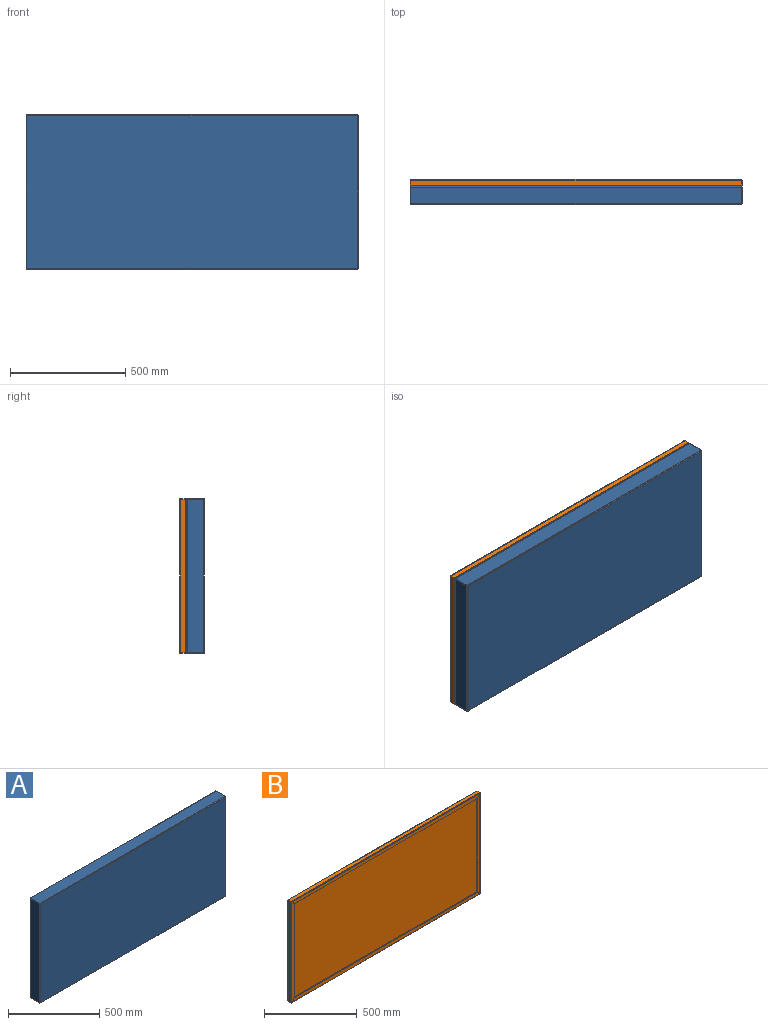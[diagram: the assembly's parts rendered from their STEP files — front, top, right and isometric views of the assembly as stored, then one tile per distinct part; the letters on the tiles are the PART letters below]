
ASSEMBLY  parts=2 mates=1
PART A: 78 faces, bbox 1439x79x669 mm
  f0: plane 2.28x2mm, normal (0,-1,0), area 4.6mm2, adj f3,f4,f5,f7
  f1: plane 2.28x2mm, normal (0,-1,0), area 4.6mm2, adj f2,f4,f5,f6
  f2: plane 70.4x2mm, normal (-1,0,0), area 140.8mm2, adj f1,f4,f5,f36
  f3: plane 70.4x2mm, normal (1,0,0), area 140.8mm2, adj f0,f4,f5,f37
  f4: plane 1434.96x70.4mm, normal (0,0,-1), area 101021.2mm2, adj f0,f1,f2,f3,f8,f38
  f5: plane 1434.96x70.4mm, normal (0,0,1), area 101021.2mm2, adj f0,f1,f2,f3,f9,f39
  f6: plane 4.3x4.3mm, normal (-1,0,0), area 10.4mm2, adj f1,f8,f9,f51
  f7: plane 4.3x4.3mm, normal (1,0,0), area 10.4mm2, adj f0,f8,f9,f41
  f8: cylinder r=4.3mm len=1430.4mm, axis (-1,0,0), area 9661.5mm2, adj f4,f6,f7,f10
  f9: cylinder r=2.3mm len=1430.4mm, axis (-1,0,0), area 5167.8mm2, adj f5,f6,f7,f11
  f10: plane 1430.4x660.4mm, normal (0,-1,0), area 944636.2mm2, adj f8,f29,f42,f52
  f11: plane 1430.4x660.4mm, normal (0,1,0), area 944636.2mm2, adj f9,f30,f43,f53
  f12: plane 2.28x2mm, normal (0,-1,0), area 4.6mm2, adj f15,f16,f17,f27
  f13: plane 2.28x2mm, normal (0,-1,0), area 4.6mm2, adj f14,f16,f17,f28
  f14: plane 70.4x2mm, normal (1,0,0), area 140.8mm2, adj f13,f16,f17,f24
  f15: plane 70.4x2mm, normal (-1,0,0), area 140.8mm2, adj f12,f16,f17,f23
  f16: plane 1434.96x70.4mm, normal (0,0,1), area 101021.2mm2, adj f12,f13,f14,f15,f25,f29
  f17: plane 1434.96x70.4mm, normal (0,0,-1), area 101021.2mm2, adj f12,f13,f14,f15,f26,f30
  f18: plane 1388.97x2mm, normal (0,0,-1), area 2777.9mm2, adj f19,f20,f21,f22
  f19: plane 20.7x20.7mm, normal (-0.71,0,-0.71), area 58.5mm2, adj f18,f21,f22,f23
  f20: plane 20.7x20.7mm, normal (0.71,0,-0.71), area 58.5mm2, adj f18,f21,f22,f24
  f21: plane 1430.37x20.7mm, normal (0,1,0), area 29180.2mm2, adj f18,f19,f20,f25
  f22: plane 1430.37x20.7mm, normal (0,-1,0), area 29180.2mm2, adj f18,f19,f20,f26
  f23: bspline ~4.3x4.3mm, area 11.6mm2, adj f15,f19,f25,f26
  f24: bspline ~4.3x4.3mm, area 11.5mm2, adj f14,f20,f25,f26
  f25: cylinder r=4.3mm len=1434.96mm, axis (-1,0,0), area 9681.1mm2, adj f16,f21,f23,f24
  f26: cylinder r=2.3mm len=1434.96mm, axis (-1,0,0), area 5178.3mm2, adj f17,f22,f23,f24
  f27: plane 4.3x4.3mm, normal (-1,0,0), area 10.4mm2, adj f12,f29,f30,f50
  f28: plane 4.3x4.3mm, normal (1,0,0), area 10.4mm2, adj f13,f29,f30,f40
  f29: cylinder r=4.3mm len=1430.4mm, axis (-1,0,0), area 9661.5mm2, adj f10,f16,f27,f28
  f30: cylinder r=2.3mm len=1430.4mm, axis (-1,0,0), area 5167.8mm2, adj f11,f17,f27,f28
  f31: plane 1388.97x2mm, normal (0,0,1), area 2777.9mm2, adj f32,f33,f34,f35
  f32: plane 20.7x20.7mm, normal (0.71,0,0.71), area 58.5mm2, adj f31,f34,f35,f37
  f33: plane 20.7x20.7mm, normal (-0.71,0,0.71), area 58.5mm2, adj f31,f34,f35,f36
  f34: plane 1430.37x20.7mm, normal (0,1,0), area 29180.2mm2, adj f31,f32,f33,f38
  f35: plane 1430.37x20.7mm, normal (0,-1,0), area 29180.2mm2, adj f31,f32,f33,f39
  f36: bspline ~4.3x4.3mm, area 11.5mm2, adj f2,f33,f38,f39
  f37: bspline ~4.3x4.3mm, area 11.6mm2, adj f3,f32,f38,f39
  f38: cylinder r=4.3mm len=1434.96mm, axis (-1,0,0), area 9681.1mm2, adj f4,f34,f36,f37
  f39: cylinder r=2.3mm len=1434.96mm, axis (-1,0,0), area 5178.2mm2, adj f5,f35,f36,f37
  f40: plane 4.3x4.3mm, normal (0,0,1), area 10.4mm2, adj f28,f42,f43,f44
  f41: plane 4.3x4.3mm, normal (0,0,-1), area 10.4mm2, adj f7,f42,f43,f45
  f42: cylinder r=4.3mm len=660.4mm, axis (0,0,1), area 4460.6mm2, adj f10,f40,f41,f48
  f43: cylinder r=2.3mm len=660.4mm, axis (0,0,1), area 2385.9mm2, adj f11,f40,f41,f49
  f44: plane 2.28x2mm, normal (0,-1,0), area 4.6mm2, adj f40,f47,f48,f49
  f45: plane 2.28x2mm, normal (0,-1,0), area 4.6mm2, adj f41,f46,f48,f49
  f46: plane 70.4x2mm, normal (0,0,-1), area 140.8mm2, adj f45,f48,f49,f60
  f47: plane 70.4x2mm, normal (0,0,1), area 140.8mm2, adj f44,f48,f49,f59
  f48: plane 664.96x70.4mm, normal (1,0,0), area 46813.2mm2, adj f42,f44,f45,f46,f47,f61
  f49: plane 664.96x70.4mm, normal (-1,0,0), area 46813.2mm2, adj f43,f44,f45,f46,f47,f62
  f50: plane 4.3x4.3mm, normal (0,0,1), area 10.4mm2, adj f27,f52,f53,f64
  f51: plane 4.3x4.3mm, normal (0,0,-1), area 10.4mm2, adj f6,f52,f53,f63
  f52: cylinder r=4.3mm len=660.4mm, axis (0,0,1), area 4460.6mm2, adj f10,f50,f51,f67
  f53: cylinder r=2.3mm len=660.4mm, axis (0,0,1), area 2385.9mm2, adj f11,f50,f51,f68
  f54: plane 618.97x2mm, normal (-1,0,0), area 1237.9mm2, adj f55,f56,f57,f58
  f55: plane 20.7x20.7mm, normal (-0.71,0,0.71), area 58.5mm2, adj f54,f57,f58,f59
  f56: plane 20.7x20.7mm, normal (-0.71,0,-0.71), area 58.5mm2, adj f54,f57,f58,f60
  f57: plane 660.37x20.7mm, normal (0,1,0), area 13241.2mm2, adj f54,f55,f56,f61
  f58: plane 660.37x20.7mm, normal (0,-1,0), area 13241.2mm2, adj f54,f55,f56,f62
  f59: bspline ~4.3x4.3mm, area 11.6mm2, adj f47,f55,f61,f62
  f60: bspline ~4.3x4.3mm, area 11.5mm2, adj f46,f56,f61,f62
  f61: cylinder r=4.3mm len=664.96mm, axis (0,0,1), area 4480.2mm2, adj f48,f57,f59,f60
  f62: cylinder r=2.3mm len=664.96mm, axis (0,0,1), area 2396.4mm2, adj f49,f58,f59,f60
  f63: plane 2.28x2mm, normal (0,-1,0), area 4.6mm2, adj f51,f66,f67,f68
  f64: plane 2.28x2mm, normal (0,-1,0), area 4.6mm2, adj f50,f65,f67,f68
  f65: plane 70.4x2mm, normal (0,0,1), area 140.8mm2, adj f64,f67,f68,f74
  f66: plane 70.4x2mm, normal (0,0,-1), area 140.8mm2, adj f63,f67,f68,f75
  f67: plane 664.96x70.4mm, normal (-1,0,0), area 46813.2mm2, adj f52,f63,f64,f65,f66,f76
  f68: plane 664.96x70.4mm, normal (1,0,0), area 46813.2mm2, adj f53,f63,f64,f65,f66,f77
  f69: plane 618.97x2mm, normal (1,0,0), area 1237.9mm2, adj f70,f71,f72,f73
  f70: plane 20.7x20.7mm, normal (0.71,0,-0.71), area 58.5mm2, adj f69,f72,f73,f75
  f71: plane 20.7x20.7mm, normal (0.71,0,0.71), area 58.5mm2, adj f69,f72,f73,f74
  f72: plane 660.37x20.7mm, normal (0,1,0), area 13241.2mm2, adj f69,f70,f71,f76
  f73: plane 660.37x20.7mm, normal (0,-1,0), area 13241.2mm2, adj f69,f70,f71,f77
  f74: bspline ~4.3x4.3mm, area 11.5mm2, adj f65,f71,f76,f77
  f75: bspline ~4.3x4.3mm, area 11.6mm2, adj f66,f70,f76,f77
  f76: cylinder r=4.3mm len=664.96mm, axis (0,0,1), area 4480.2mm2, adj f67,f72,f74,f75
  f77: cylinder r=2.3mm len=664.96mm, axis (0,0,1), area 2396.4mm2, adj f68,f73,f74,f75
PART B: 78 faces, bbox 1439x29x669 mm
  f0: plane 2.28x2mm, normal (0,1,0), area 4.6mm2, adj f3,f4,f5,f6
  f1: plane 2.28x2mm, normal (0,1,0), area 4.6mm2, adj f2,f4,f5,f7
  f2: plane 20.4x2mm, normal (1,0,0), area 40.8mm2, adj f1,f4,f5,f37
  f3: plane 20.4x2mm, normal (-1,0,0), area 40.8mm2, adj f0,f4,f5,f36
  f4: plane 1434.96x20.4mm, normal (0,0,-1), area 29273.2mm2, adj f0,f1,f2,f3,f8,f38
  f5: plane 1434.96x20.4mm, normal (0,0,1), area 29273.2mm2, adj f0,f1,f2,f3,f9,f39
  f6: plane 4.3x4.3mm, normal (-1,0,0), area 10.4mm2, adj f0,f8,f9,f47
  f7: plane 4.3x4.3mm, normal (1,0,0), area 10.4mm2, adj f1,f8,f9,f66
  f8: cylinder r=4.3mm len=1430.4mm, axis (-1,0,0), area 9661.5mm2, adj f4,f6,f7,f10
  f9: cylinder r=2.3mm len=1430.4mm, axis (-1,0,0), area 5167.8mm2, adj f5,f6,f7,f11
  f10: plane 1430.4x660.4mm, normal (0,1,0), area 944636.2mm2, adj f8,f29,f48,f67
  f11: plane 1430.4x660.4mm, normal (0,-1,0), area 944636.2mm2, adj f9,f30,f49,f68
  f12: plane 2.28x2mm, normal (0,1,0), area 4.6mm2, adj f15,f16,f17,f28
  f13: plane 2.28x2mm, normal (0,1,0), area 4.6mm2, adj f14,f16,f17,f27
  f14: plane 20.4x2mm, normal (-1,0,0), area 40.8mm2, adj f13,f16,f17,f23
  f15: plane 20.4x2mm, normal (1,0,0), area 40.8mm2, adj f12,f16,f17,f24
  f16: plane 1434.96x20.4mm, normal (0,0,1), area 29273.2mm2, adj f12,f13,f14,f15,f25,f29
  f17: plane 1434.96x20.4mm, normal (0,0,-1), area 29273.2mm2, adj f12,f13,f14,f15,f26,f30
  f18: plane 1388.97x2mm, normal (0,0,-1), area 2777.9mm2, adj f19,f20,f21,f22
  f19: plane 20.7x20.7mm, normal (0.71,0,-0.71), area 58.5mm2, adj f18,f21,f22,f24
  f20: plane 20.7x20.7mm, normal (-0.71,0,-0.71), area 58.5mm2, adj f18,f21,f22,f23
  f21: plane 1430.37x20.7mm, normal (0,-1,0), area 29180.2mm2, adj f18,f19,f20,f25
  f22: plane 1430.37x20.7mm, normal (0,1,0), area 29180.2mm2, adj f18,f19,f20,f26
  f23: bspline ~4.3x4.3mm, area 11.5mm2, adj f14,f20,f25,f26
  f24: bspline ~4.3x4.3mm, area 11.6mm2, adj f15,f19,f25,f26
  f25: cylinder r=4.3mm len=1434.96mm, axis (-1,0,0), area 9681.1mm2, adj f16,f21,f23,f24
  f26: cylinder r=2.3mm len=1434.96mm, axis (-1,0,0), area 5178.2mm2, adj f17,f22,f23,f24
  f27: plane 4.3x4.3mm, normal (-1,0,0), area 10.4mm2, adj f13,f29,f30,f46
  f28: plane 4.3x4.3mm, normal (1,0,0), area 10.4mm2, adj f12,f29,f30,f65
  f29: cylinder r=4.3mm len=1430.4mm, axis (-1,0,0), area 9661.5mm2, adj f10,f16,f27,f28
  f30: cylinder r=2.3mm len=1430.4mm, axis (-1,0,0), area 5167.8mm2, adj f11,f17,f27,f28
  f31: plane 1388.97x2mm, normal (0,0,1), area 2777.9mm2, adj f32,f33,f34,f35
  f32: plane 20.7x20.7mm, normal (-0.71,0,0.71), area 58.5mm2, adj f31,f34,f35,f36
  f33: plane 20.7x20.7mm, normal (0.71,0,0.71), area 58.5mm2, adj f31,f34,f35,f37
  f34: plane 1430.37x20.7mm, normal (0,-1,0), area 29180.2mm2, adj f31,f32,f33,f38
  f35: plane 1430.37x20.7mm, normal (0,1,0), area 29180.2mm2, adj f31,f32,f33,f39
  f36: bspline ~4.3x4.3mm, area 11.6mm2, adj f3,f32,f38,f39
  f37: bspline ~4.3x4.3mm, area 11.5mm2, adj f2,f33,f38,f39
  f38: cylinder r=4.3mm len=1434.96mm, axis (-1,0,0), area 9681.1mm2, adj f4,f34,f36,f37
  f39: cylinder r=2.3mm len=1434.96mm, axis (-1,0,0), area 5178.3mm2, adj f5,f35,f36,f37
  f40: plane 2.28x2mm, normal (0,1,0), area 4.6mm2, adj f43,f44,f45,f46
  f41: plane 2.28x2mm, normal (0,1,0), area 4.6mm2, adj f42,f44,f45,f47
  f42: plane 20.4x2mm, normal (0,0,-1), area 40.8mm2, adj f41,f44,f45,f51
  f43: plane 20.4x2mm, normal (0,0,1), area 40.8mm2, adj f40,f44,f45,f50
  f44: plane 664.96x20.4mm, normal (-1,0,0), area 13565.2mm2, adj f40,f41,f42,f43,f48,f52
  f45: plane 664.96x20.4mm, normal (1,0,0), area 13565.2mm2, adj f40,f41,f42,f43,f49,f53
  f46: plane 4.3x4.3mm, normal (0,0,1), area 10.4mm2, adj f27,f40,f48,f49
  f47: plane 4.3x4.3mm, normal (0,0,-1), area 10.4mm2, adj f6,f41,f48,f49
  f48: cylinder r=4.3mm len=660.4mm, axis (0,0,1), area 4460.6mm2, adj f10,f44,f46,f47
  f49: cylinder r=2.3mm len=660.4mm, axis (0,0,1), area 2385.9mm2, adj f11,f45,f46,f47
  f50: bspline ~4.3x4.3mm, area 11.6mm2, adj f43,f52,f53,f55
  f51: bspline ~4.3x4.3mm, area 11.5mm2, adj f42,f52,f53,f56
  f52: cylinder r=4.3mm len=664.96mm, axis (0,0,1), area 4480.2mm2, adj f44,f50,f51,f57
  f53: cylinder r=2.3mm len=664.96mm, axis (0,0,1), area 2396.4mm2, adj f45,f50,f51,f58
  f54: plane 618.97x2mm, normal (1,0,0), area 1237.9mm2, adj f55,f56,f57,f58
  f55: plane 20.7x20.7mm, normal (0.71,0,0.71), area 58.5mm2, adj f50,f54,f57,f58
  f56: plane 20.7x20.7mm, normal (0.71,0,-0.71), area 58.5mm2, adj f51,f54,f57,f58
  f57: plane 660.37x20.7mm, normal (0,-1,0), area 13241.2mm2, adj f52,f54,f55,f56
  f58: plane 660.37x20.7mm, normal (0,1,0), area 13241.2mm2, adj f53,f54,f55,f56
  f59: plane 2.28x2mm, normal (0,1,0), area 4.6mm2, adj f62,f63,f64,f66
  f60: plane 2.28x2mm, normal (0,1,0), area 4.6mm2, adj f61,f63,f64,f65
  f61: plane 20.4x2mm, normal (0,0,1), area 40.8mm2, adj f60,f63,f64,f69
  f62: plane 20.4x2mm, normal (0,0,-1), area 40.8mm2, adj f59,f63,f64,f70
  f63: plane 664.96x20.4mm, normal (1,0,0), area 13565.2mm2, adj f59,f60,f61,f62,f67,f71
  f64: plane 664.96x20.4mm, normal (-1,0,0), area 13565.2mm2, adj f59,f60,f61,f62,f68,f72
  f65: plane 4.3x4.3mm, normal (0,0,1), area 10.4mm2, adj f28,f60,f67,f68
  f66: plane 4.3x4.3mm, normal (0,0,-1), area 10.4mm2, adj f7,f59,f67,f68
  f67: cylinder r=4.3mm len=660.4mm, axis (0,0,1), area 4460.6mm2, adj f10,f63,f65,f66
  f68: cylinder r=2.3mm len=660.4mm, axis (0,0,1), area 2385.9mm2, adj f11,f64,f65,f66
  f69: bspline ~4.3x4.3mm, area 11.5mm2, adj f61,f71,f72,f75
  f70: bspline ~4.3x4.3mm, area 11.6mm2, adj f62,f71,f72,f74
  f71: cylinder r=4.3mm len=664.96mm, axis (0,0,1), area 4480.2mm2, adj f63,f69,f70,f76
  f72: cylinder r=2.3mm len=664.96mm, axis (0,0,1), area 2396.4mm2, adj f64,f69,f70,f77
  f73: plane 618.97x2mm, normal (-1,0,0), area 1237.9mm2, adj f74,f75,f76,f77
  f74: plane 20.7x20.7mm, normal (-0.71,0,-0.71), area 58.5mm2, adj f70,f73,f76,f77
  f75: plane 20.7x20.7mm, normal (-0.71,0,0.71), area 58.5mm2, adj f69,f73,f76,f77
  f76: plane 660.37x20.7mm, normal (0,-1,0), area 13241.2mm2, adj f71,f73,f74,f75
  f77: plane 660.37x20.7mm, normal (0,1,0), area 13241.2mm2, adj f72,f73,f74,f75
PLACE A at identity
PLACE B t=(0,4,0)mm
MATE fastened B.f21 <-> A.f21  axis (0,-1,0) through (0,2,319.9)mm
